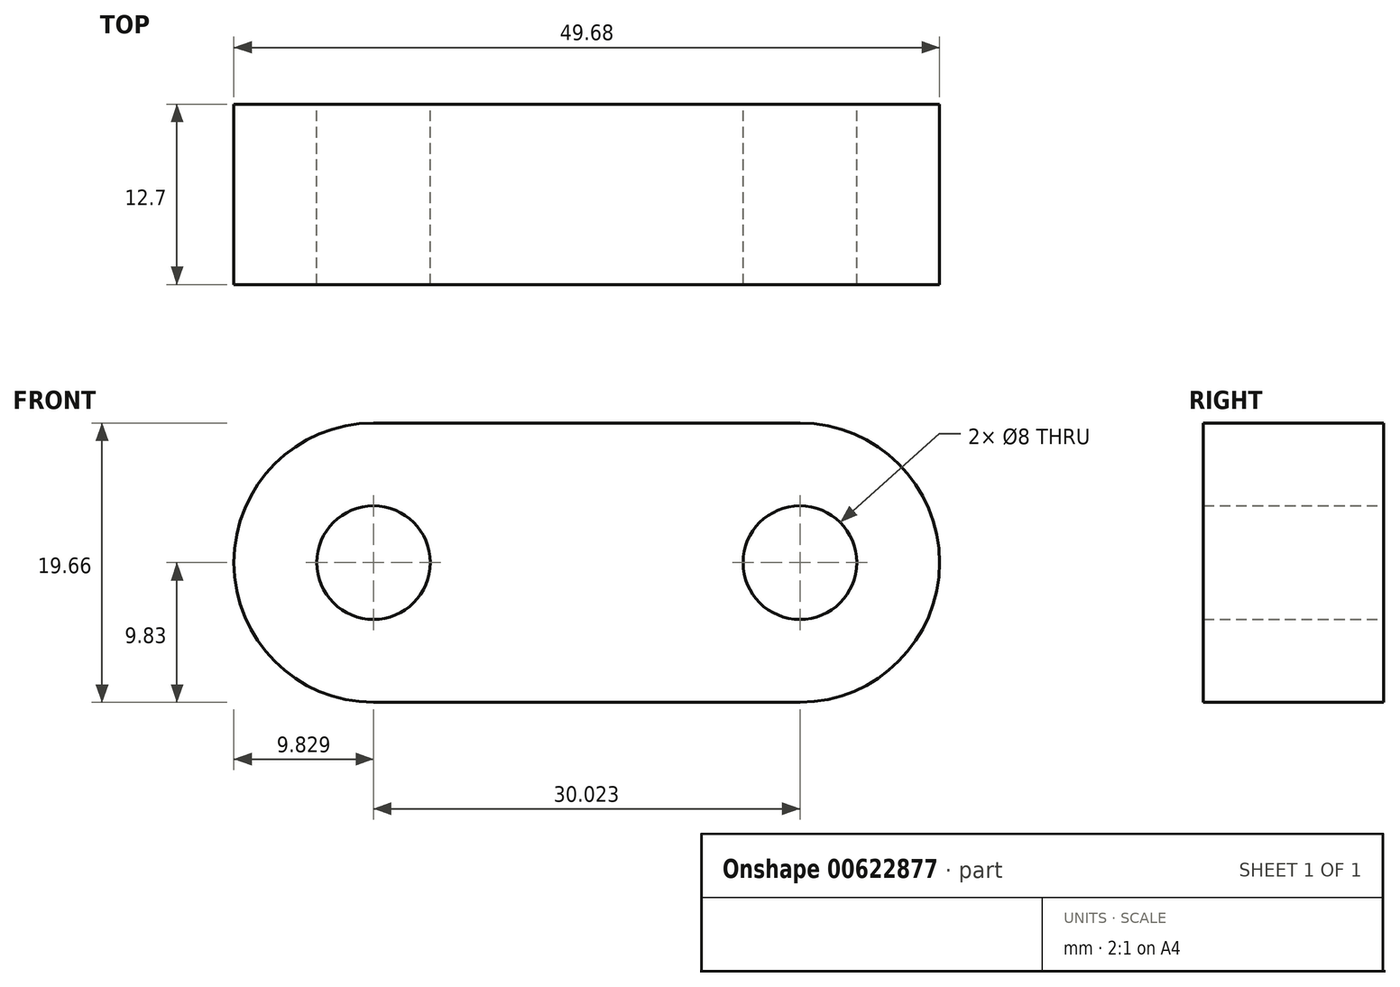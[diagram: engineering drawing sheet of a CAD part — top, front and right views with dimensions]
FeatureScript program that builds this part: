
annotation { "Feature Type Name" : "Feature", "Feature Type Description" : "" }
export const myFeature = defineFeature(function(context is Context, id is Id, definition is map)
    precondition{}
    {
        {
            var Q0;
            Q0=qCreatedBy(makeId("Front.planeOp"),FACE);
            var sketch = newSketch(context, id + "F0", { "sketchPlane" : qUnion([Q0])});
            skLineSegment(sketch, "E0", {"start": v(-15.01, 0) * mm, "end": v(0, 0) * mm});
            skLineSegment(sketch, "E1", {"start": v(0, 19.14) * mm, "end": v(0, -22.34) * mm});
            skArc(sketch, "E2", {"start": v(-15.01, 9.83) * mm, "mid": v(-24.84, 0) * mm, "end": v(-15.01, -9.83) * mm});
            skLineSegment(sketch, "E3.0", {"start": v(-15.01, 9.83) * mm, "end": v(0, 9.83) * mm});
            skCircle(sketch, "E4", {"center": v(-15.01, 0) * mm, "radius": 4 * mm});
            skLineSegment(sketch, "E5", {"start": v(-15.01, -9.83) * mm, "end": v(0, -9.83) * mm});
            skLineSegment(sketch, "E6.MirrorCS", {"start": v(15.01, 0) * mm, "end": v(0, 0) * mm});
            skLineSegment(sketch, "E7.MirrorCS", {"start": v(15.01, 9.83) * mm, "end": v(0, 9.83) * mm});
            skLineSegment(sketch, "E8.MirrorCS", {"start": v(15.01, -9.83) * mm, "end": v(0, -9.83) * mm});
            skCircle(sketch, "E9.MirrorC", {"center": v(15.01, 0) * mm, "radius": 4 * mm});
            skArc(sketch, "E10.MirrorCS", {"start": v(15.01, 9.83) * mm, "mid": v(24.84, 0) * mm, "end": v(15.01, -9.83) * mm});
            skSolve(sketch);
        }
        {
            var Q0;
            Q0=makeQuery(id+"F0.imprint","IMPRINT",FACE,{"disambiguationData":[TD([[makeQuery(id+"F0.imprint","IMPRINT",EDGE,{"derivedFrom":sQuery(id+"F0.wireOp",EDGE,"E2")}),1.0]])]});
            var Q1;
            {var subQ1=sQuery(id+"F0.wireOp",EDGE,"E7.MirrorCS");Q1=makeQuery(id+"F0.imprint","IMPRINT",FACE,{"disambiguationData":[TD([[makeQuery(id+"F0.imprint","IMPRINT",EDGE,{"derivedFrom":subQ1}),1.0]])]});}
            extrude(context, id + "F1", {"entities" : qUnion([Q0, Q1]), "endBound" : BoundingType.SYMMETRIC, "depth" : 12.7 * mm, "offsetDistance" : 25.4 * mm});
        }
    });
